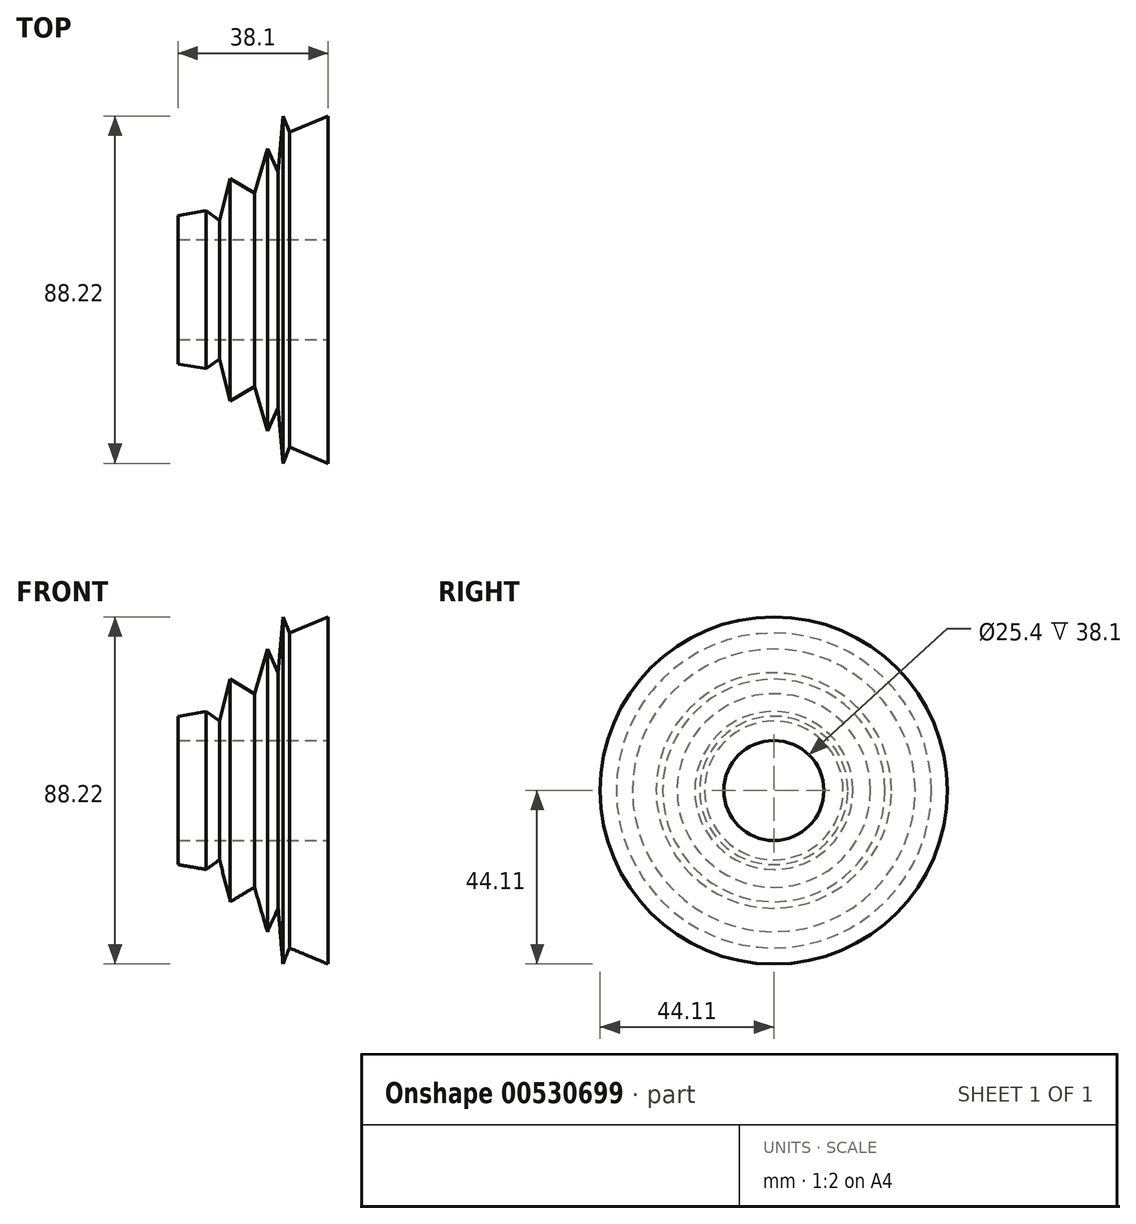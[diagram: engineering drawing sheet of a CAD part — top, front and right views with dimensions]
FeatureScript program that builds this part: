
annotation { "Feature Type Name" : "Feature", "Feature Type Description" : "" }
export const myFeature = defineFeature(function(context is Context, id is Id, definition is map)
    precondition{}
    {
        {
            var Q0;
            Q0=qCreatedBy(makeId("Front.planeOp"),FACE);
            var sketch = newSketch(context, id + "F0", { "sketchPlane" : qUnion([Q0])});
            skLineSegment(sketch, "E0", {"start": v(0, 0) * mm, "end": v(-71.42, 0) * mm});
            skLineSegment(sketch, "E1", {"start": v(0, 12.7) * mm, "end": v(-38.1, 12.7) * mm});
            skLineSegment(sketch, "E2", {"start": v(-38.1, 12.7) * mm, "end": v(-38.1, 18.85) * mm});
            skLineSegment(sketch, "E3", {"start": v(-38.1, 18.85) * mm, "end": v(-31, 20.07) * mm});
            skLineSegment(sketch, "E4", {"start": v(-31, 20.07) * mm, "end": v(-27.58, 17.62) * mm});
            skLineSegment(sketch, "E5", {"start": v(-27.58, 17.62) * mm, "end": v(-24.85, 28.27) * mm});
            skLineSegment(sketch, "E6", {"start": v(-24.85, 28.27) * mm, "end": v(-18.7, 24.58) * mm});
            skLineSegment(sketch, "E7", {"start": v(-18.7, 24.58) * mm, "end": v(-15.43, 35.92) * mm});
            skLineSegment(sketch, "E8", {"start": v(-15.43, 35.92) * mm, "end": v(-12.7, 29.9) * mm});
            skLineSegment(sketch, "E9", {"start": v(-12.7, 29.9) * mm, "end": v(-11.47, 44.1) * mm});
            skLineSegment(sketch, "E10", {"start": v(-11.47, 44.1) * mm, "end": v(-9.83, 40.01) * mm});
            skLineSegment(sketch, "E11", {"start": v(-9.83, 40.01) * mm, "end": v(0, 44.1) * mm});
            skLineSegment(sketch, "E12", {"start": v(0, 44.1) * mm, "end": v(0, 12.7) * mm});
            skSolve(sketch);
        }
        {
            var Q0;
            Q0 = qSketchRegion(id + "F0", true);
            var Q1;
            Q1=sQuery(id+"F0.wireOp",EDGE,"E0");
            revolve(context, id + "F1", {"entities" : qUnion([Q0]), "axis" : qUnion([Q1]), "revolveType" : RevolveType.FULL});
        }
    });
